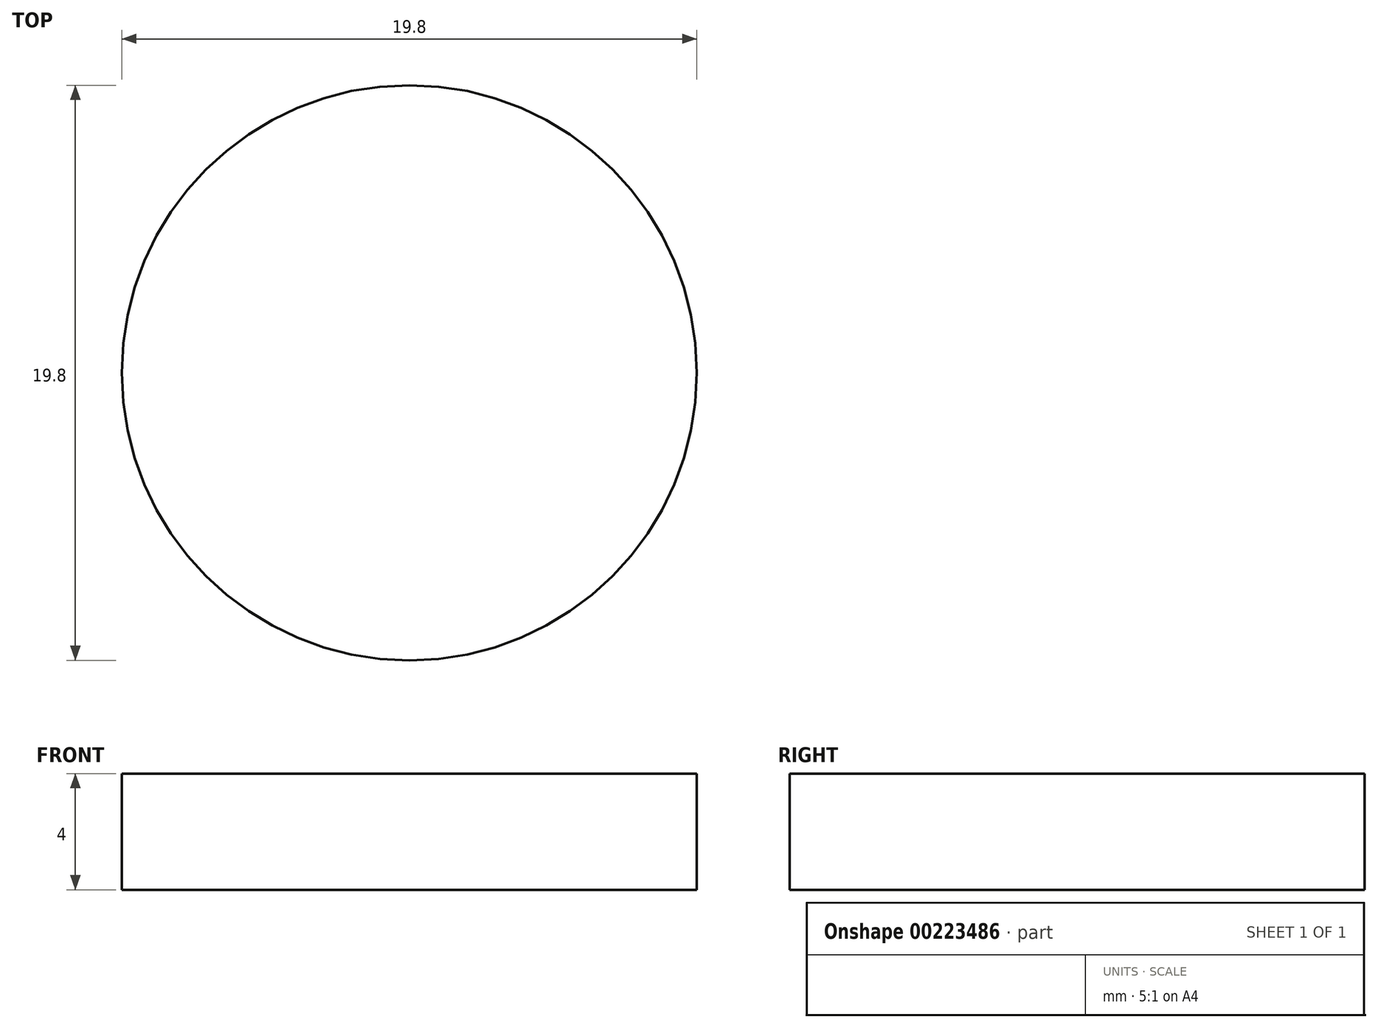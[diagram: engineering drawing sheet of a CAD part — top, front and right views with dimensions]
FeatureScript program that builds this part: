
annotation { "Feature Type Name" : "Feature", "Feature Type Description" : "" }
export const myFeature = defineFeature(function(context is Context, id is Id, definition is map)
    precondition{}
    {
        {
            assignVariable(context, id + "F0", {"name" : "PlungerHeight", "anyValue" : 6 - 2});
        }
        {
            var Q0;
            Q0=qCreatedBy(makeId("Top.planeOp"),FACE);
            var sketch = newSketch(context, id + "F1", { "sketchPlane" : qUnion([Q0])});
            skCircle(sketch, "E0", {"center": v(0, 0) * mm, "radius": 9.9 * mm});
            skSolve(sketch);
        }
        {
            var Q0;
            Q0 = qSketchRegion(id + "F1", true);
            extrude(context, id + "F2", {"entities" : qUnion([Q0]), "depth" : (getVariable(context, 'PlungerHeight')) * mm});
        }
    });
